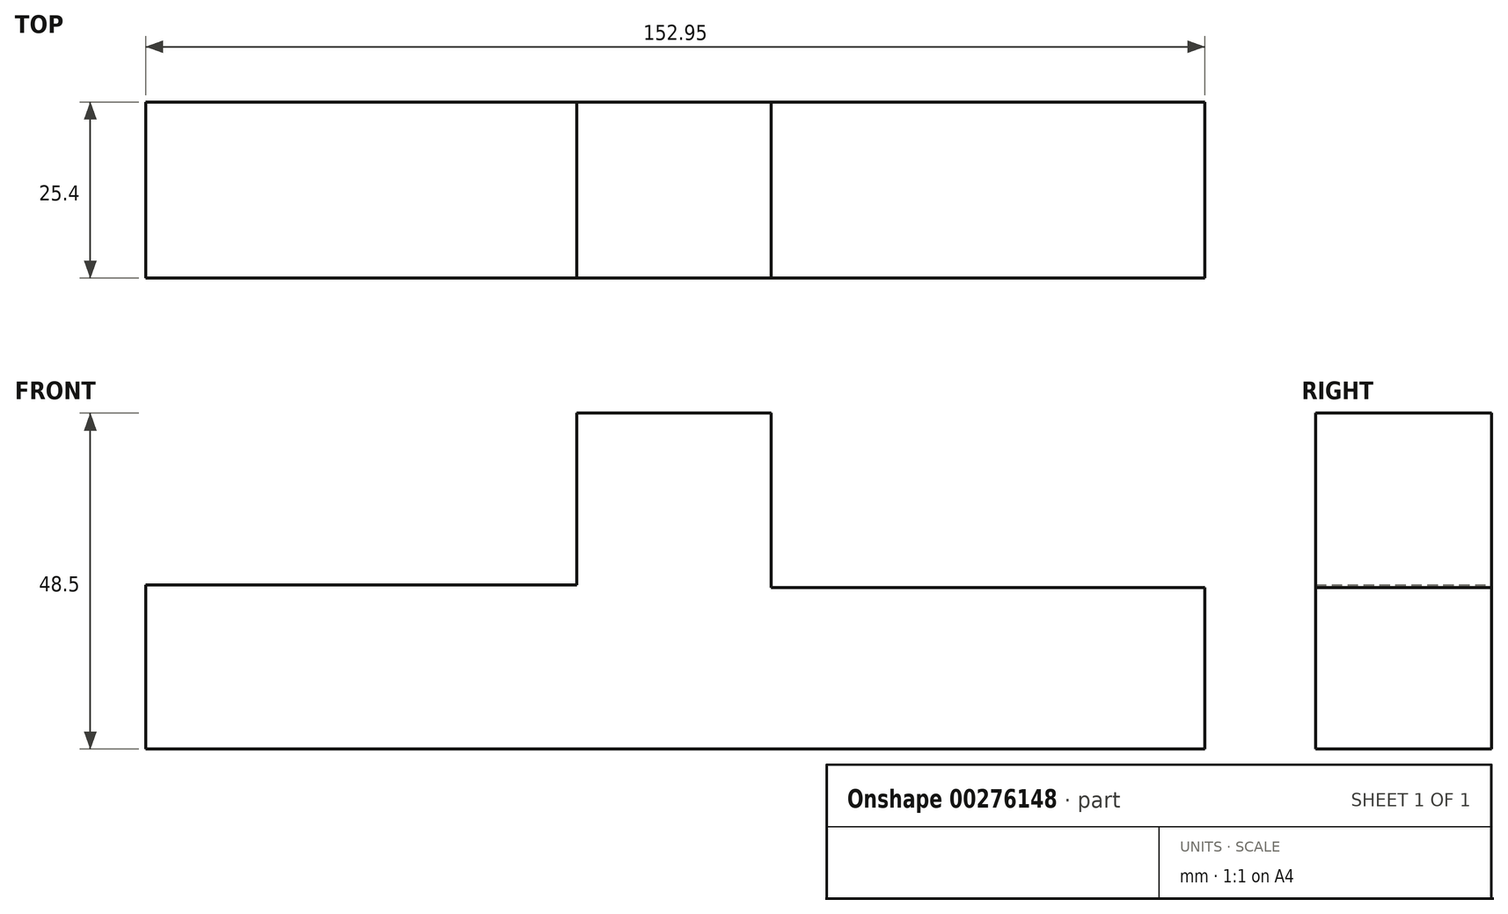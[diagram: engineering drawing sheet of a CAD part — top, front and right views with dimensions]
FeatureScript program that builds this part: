
annotation { "Feature Type Name" : "Feature", "Feature Type Description" : "" }
export const myFeature = defineFeature(function(context is Context, id is Id, definition is map)
    precondition{}
    {
        {
            var Q0;
            Q0=qCreatedBy(makeId("Front.planeOp"),FACE);
            var sketch = newSketch(context, id + "F0", { "sketchPlane" : qUnion([Q0])});
            skLineSegment(sketch, "E0", {"start": v(76.76, 0) * mm, "end": v(-76.2, 0) * mm});
            skLineSegment(sketch, "E1", {"start": v(-76.2, 0) * mm, "end": v(-76.2, 23.68) * mm});
            skLineSegment(sketch, "E2", {"start": v(-76.2, 23.68) * mm, "end": v(-13.94, 23.68) * mm});
            skLineSegment(sketch, "E3", {"start": v(-13.94, 23.68) * mm, "end": v(-13.94, 48.5) * mm});
            skLineSegment(sketch, "E4", {"start": v(-13.94, 48.5) * mm, "end": v(14.13, 48.5) * mm});
            skLineSegment(sketch, "E5", {"start": v(14.13, 48.5) * mm, "end": v(14.13, 23.3) * mm});
            skLineSegment(sketch, "E6", {"start": v(14.13, 23.3) * mm, "end": v(76.76, 23.3) * mm});
            skLineSegment(sketch, "E7", {"start": v(76.76, 23.3) * mm, "end": v(76.76, 0) * mm});
            skSolve(sketch);
        }
        {
            var Q0;
            Q0 = qSketchRegion(id + "F0", true);
            extrude(context, id + "F1", {"entities" : qUnion([Q0]), "depth" : 25.4 * mm});
        }
    });
